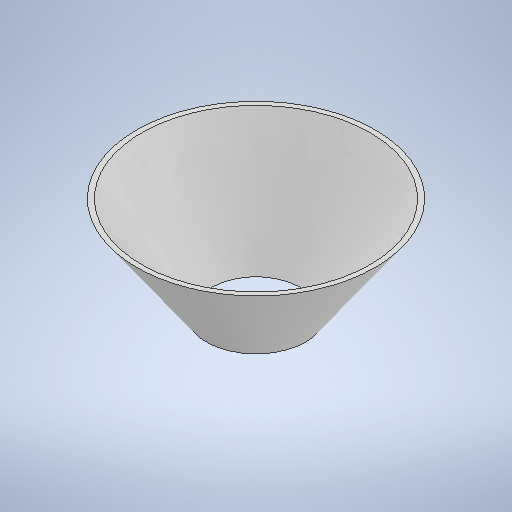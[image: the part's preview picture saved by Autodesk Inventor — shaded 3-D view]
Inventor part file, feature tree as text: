
AUTODESK INVENTOR PART (.ipt)
format: ipt  version: 2025 (Build 290162000, 162)  size: 250,880 bytes
history: native  units: mm
features: extrude x2, sketch x2
ambient origin geometry x8: Origin, YZ Plane, XZ Plane, XY Plane, X Axis, Y Axis, Z Axis, Center Point
bodies: Body1 (feature_tree)
feature tree (4):
  extrude  "Wyciągnięcie proste5"  Depth=100.0mm
  extrude  "Wyciągnięcie proste6"  Depth=100.0mm
  sketch  "Szkic6"
  sketch  "Szkic7"
